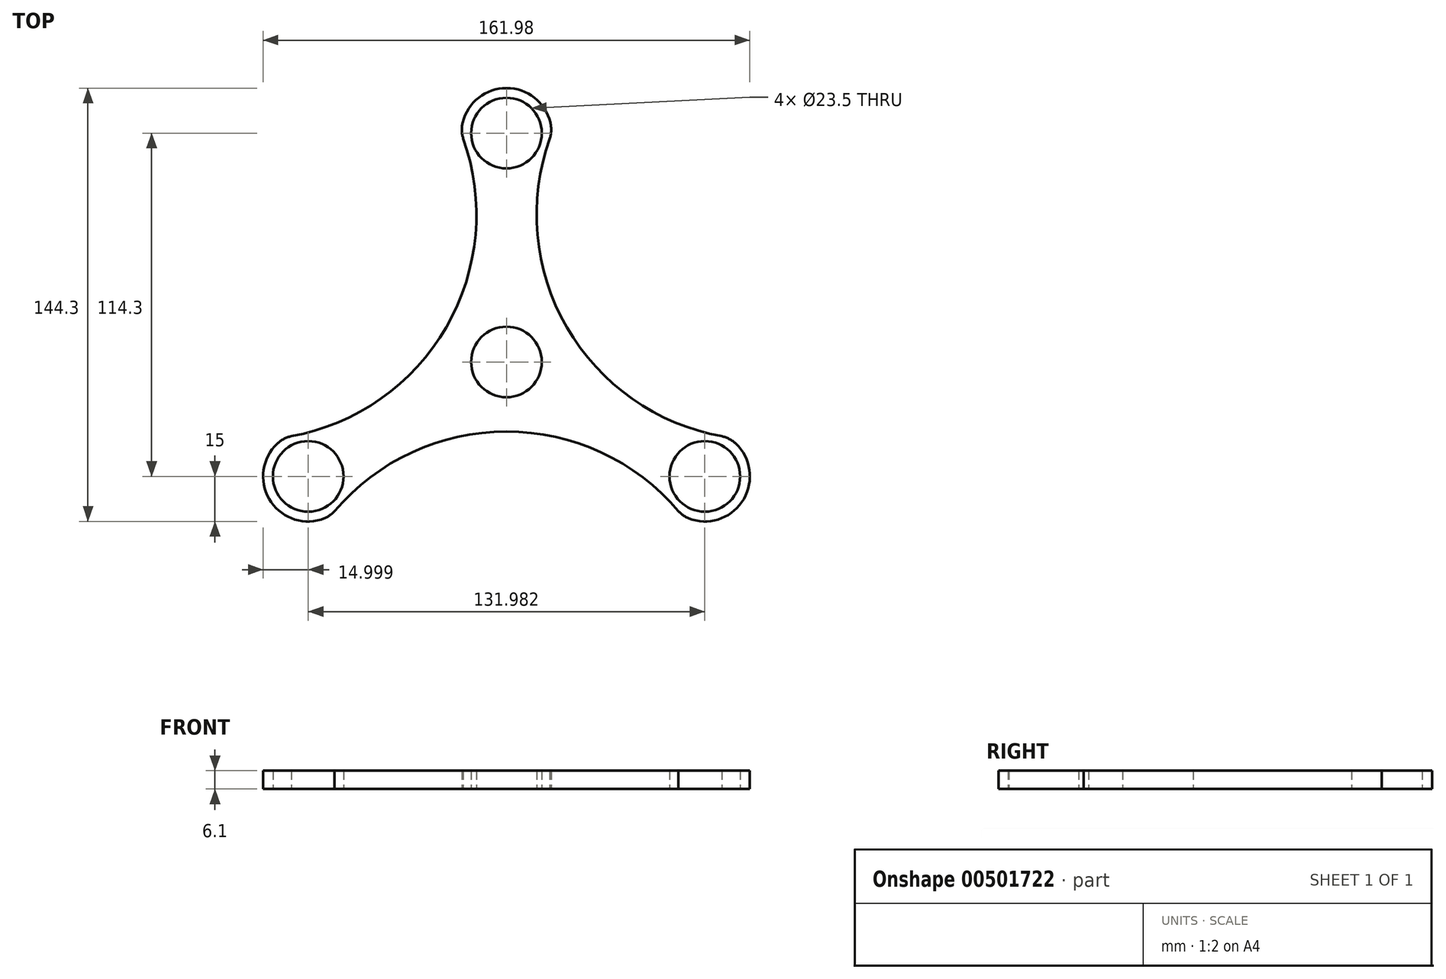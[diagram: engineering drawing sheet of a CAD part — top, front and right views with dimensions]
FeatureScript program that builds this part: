
annotation { "Feature Type Name" : "Feature", "Feature Type Description" : "" }
export const myFeature = defineFeature(function(context is Context, id is Id, definition is map)
    precondition{}
    {
        {
            var Q0;
            Q0=qCreatedBy(makeId("Top.planeOp"),FACE);
            var sketch = newSketch(context, id + "F0", { "sketchPlane" : qUnion([Q0])});
            skCircle(sketch, "E0", {"center": v(0, 76.2) * mm, "radius": 11.75 * mm});
            skCircle(sketch, "E1", {"center": v(0, 0) * mm, "radius": 11.75 * mm});
            skArc(sketch, "E2", {"start": v(14.58, 79.72) * mm, "mid": v(0, 91.2) * mm, "end": v(-14.58, 79.72) * mm});
            skPoint(sketch, "E3.visualSharp", {"position": v(-15, 76.2) * mm});
            skArc(sketch, "E3.filletArc", {"start": v(-14.58, 79.72) * mm, "mid": v(-14.85, 77.03) * mm, "end": v(-14.4, 74.37) * mm});
            skPoint(sketch, "E4.visualSharp", {"position": v(15, 76.2) * mm});
            skArc(sketch, "E4.filletArc", {"start": v(14.4, 74.37) * mm, "mid": v(14.85, 77.03) * mm, "end": v(14.58, 79.72) * mm});
            skArc(sketch, "E5", {"start": v(-71.6, -24.71) * mm, "mid": v(-20.05, 11.58) * mm, "end": v(-14.4, 74.37) * mm});
            skArc(sketch, "E6.1.0", {"start": v(57.2, -49.65) * mm, "mid": v(0, -23.16) * mm, "end": v(-57.2, -49.65) * mm});
            skCircle(sketch, "E6.1.2", {"center": v(-66, -38.1) * mm, "radius": 11.75 * mm});
            skPoint(sketch, "E6.1.3", {"position": v(-58.5, -51.1) * mm});
            skArc(sketch, "E6.1.4", {"start": v(-76.33, -27.23) * mm, "mid": v(-78.98, -45.6) * mm, "end": v(-61.74, -52.49) * mm});
            skPoint(sketch, "E6.1.5", {"position": v(-73.5, -25.1) * mm});
            skArc(sketch, "E6.1.6", {"start": v(-71.6, -24.71) * mm, "mid": v(-74.14, -25.65) * mm, "end": v(-76.33, -27.23) * mm});
            skArc(sketch, "E6.1.8", {"start": v(-61.74, -52.49) * mm, "mid": v(-59.28, -51.38) * mm, "end": v(-57.2, -49.65) * mm});
            skArc(sketch, "E6.2.0", {"start": v(14.4, 74.37) * mm, "mid": v(20.05, 11.58) * mm, "end": v(71.6, -24.71) * mm});
            skCircle(sketch, "E6.2.2", {"center": v(66, -38.1) * mm, "radius": 11.75 * mm});
            skPoint(sketch, "E6.2.3", {"position": v(73.5, -25.1) * mm});
            skArc(sketch, "E6.2.4", {"start": v(61.74, -52.49) * mm, "mid": v(78.98, -45.6) * mm, "end": v(76.33, -27.23) * mm});
            skPoint(sketch, "E6.2.5", {"position": v(58.5, -51.1) * mm});
            skArc(sketch, "E6.2.6", {"start": v(57.2, -49.65) * mm, "mid": v(59.28, -51.38) * mm, "end": v(61.74, -52.49) * mm});
            skArc(sketch, "E6.2.8", {"start": v(76.33, -27.23) * mm, "mid": v(74.14, -25.65) * mm, "end": v(71.6, -24.71) * mm});
            skSolve(sketch);
        }
        {
            var Q0;
            Q0=makeQuery(id+"F0.imprint","IMPRINT",FACE,{"disambiguationData":[TD([[makeQuery(id+"F0.imprint","IMPRINT",EDGE,{"derivedFrom":sQuery(id+"F0.wireOp",EDGE,"E0")}),-1.0]])]});
            extrude(context, id + "F1", {"entities" : qUnion([Q0]), "depth" : 6.1 * mm});
        }
    });
